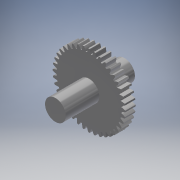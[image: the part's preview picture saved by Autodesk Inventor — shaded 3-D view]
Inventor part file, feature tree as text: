
AUTODESK INVENTOR PART (.ipt)
format: ipt  version: 2019 (Build 230136000, 136)  size: 407,040 bytes
history: native  units: mm (DEFAULTED — no unit token found)
features: other x6, plane x3, sketch x3, extrude x2
ambient origin geometry x8: Origin, YZ Plane, XZ Plane, XY Plane, X Axis, Y Axis, Z Axis, Center Point
bodies: Solid1 (feature_tree)
feature tree (14):
  extrude  "Extrusion1"  Depth=3.0mm TaperAngle=0.0deg
  plane  "Work Plane2"
  plane  "Work Plane8"
  plane  "Work Plane9"
  other  "Przekładnia walcowa"
  extrude  "Wyciągnięcie proste2"  Depth=10.0mm TaperAngle=0.0deg
  other  "Edytuj bezpośrednio1"
  sketch  "Sketch1"  dims[d0=21.0mm d1=3.0mm d2=0.0mm]
  sketch  "Sketch2"  dims[d3=20.0mm d4=10.0mm d5=0.0mm d16=13.75mm d17=0.0mm d34=0.785398mm d39=0.0mm d41=0.0mm d43=13.75mm d46=13.75mm d47=0.0mm d48=0.0mm d49=6.0mm d50=10.0mm d51=10.0mm d52=0.0mm d53=0.0mm d54=0.0mm d55=0.0mm d56=-0.3mm d57=0.0mm d58=0.0mm d59=0.3mm]
  other  "Srf1"
  sketch  "Szkic3"
  other  "Średnica podziałowa"
  other  "Przesuń1"
  other  "Przesuń2"
